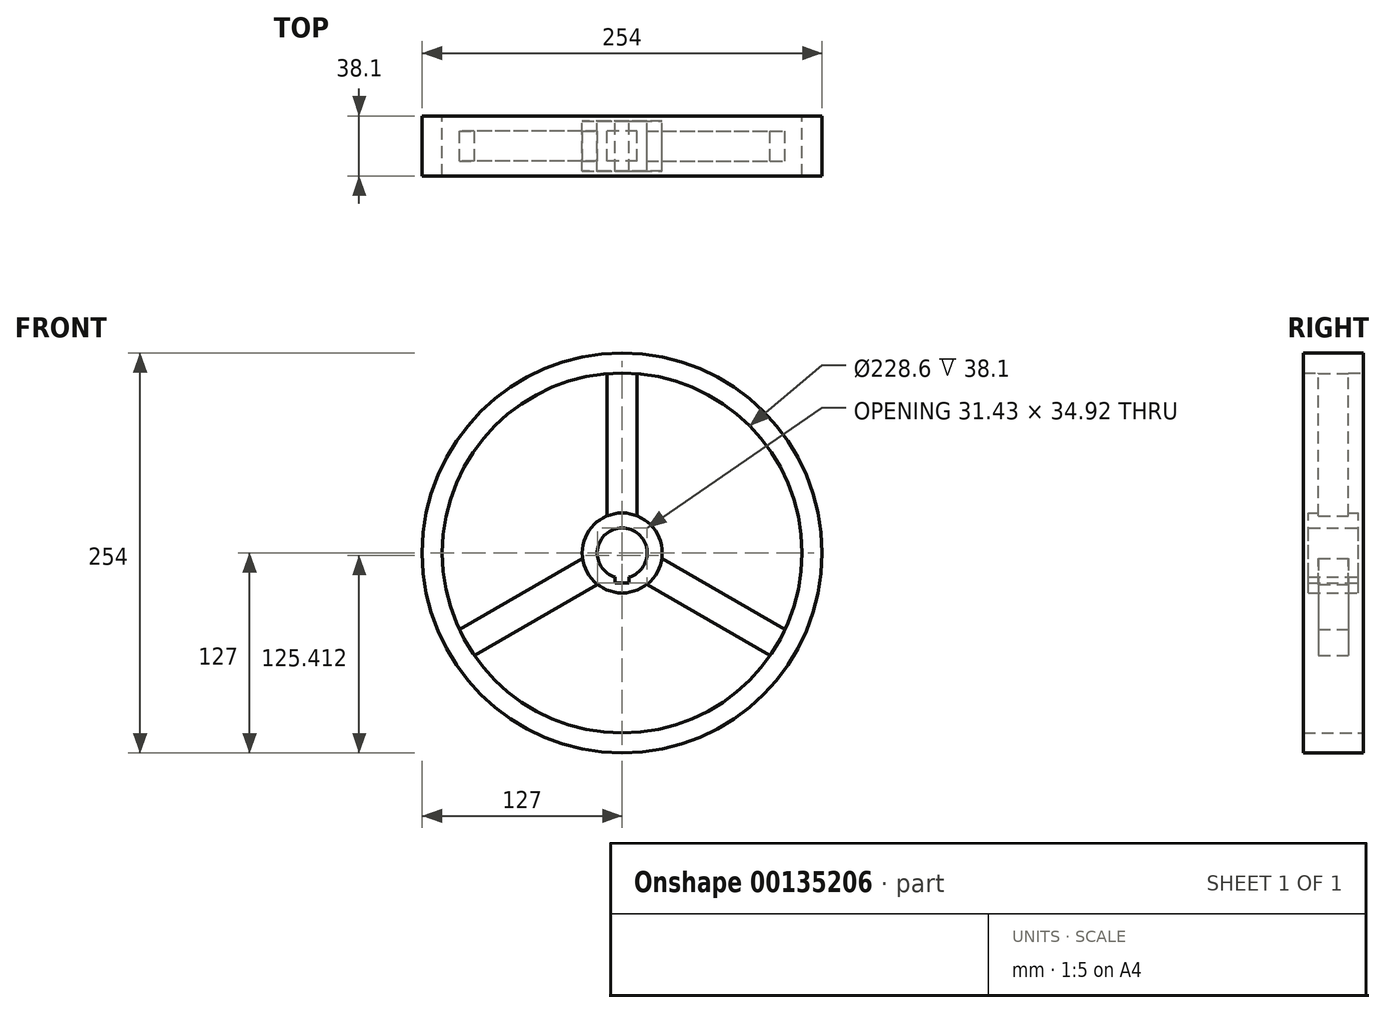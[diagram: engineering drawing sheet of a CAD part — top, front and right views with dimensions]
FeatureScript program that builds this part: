
annotation { "Feature Type Name" : "Feature", "Feature Type Description" : "" }
export const myFeature = defineFeature(function(context is Context, id is Id, definition is map)
    precondition{}
    {
        {
            var Q0;
            Q0=qCreatedBy(makeId("Front.planeOp"),FACE);
            var sketch = newSketch(context, id + "F0", { "sketchPlane" : qUnion([Q0])});
            skCircle(sketch, "E0", {"center": v(0, 0) * mm, "radius": 127 * mm});
            skCircle(sketch, "E1", {"center": v(0, 0) * mm, "radius": 114.3 * mm});
            skCircle(sketch, "E2", {"center": v(0, 0) * mm, "radius": 25.4 * mm});
            skArc(sketch, "E3", {"start": v(4.45, -15.24) * mm, "mid": v(0, 15.88) * mm, "end": v(-4.45, -15.24) * mm});
            skLineSegment(sketch, "E4", {"start": v(-9.53, 23.55) * mm, "end": v(-9.53, 113.9) * mm});
            skLineSegment(sketch, "E5", {"start": v(9.52, 23.55) * mm, "end": v(9.52, 113.9) * mm});
            skLineSegment(sketch, "E6", {"start": v(-25.15, -3.52) * mm, "end": v(-103.4, -48.7) * mm});
            skLineSegment(sketch, "E7", {"start": v(-15.63, -20.02) * mm, "end": v(-93.88, -65.2) * mm});
            skLineSegment(sketch, "E8", {"start": v(25.15, -3.52) * mm, "end": v(103.4, -48.7) * mm});
            skLineSegment(sketch, "E9", {"start": v(15.63, -20.02) * mm, "end": v(93.88, -65.2) * mm});
            skLineSegment(sketch, "E10", {"start": v(-4.45, -15.24) * mm, "end": v(-4.45, -19.05) * mm});
            skLineSegment(sketch, "E11", {"start": v(-4.44, -19.05) * mm, "end": v(4.45, -19.05) * mm});
            skLineSegment(sketch, "E12", {"start": v(4.45, -19.05) * mm, "end": v(4.45, -15.24) * mm});
            skSolve(sketch);
        }
        {
            var Q0;
            Q0 = qSketchRegion(id + "F0", true);
            extrude(context, id + "F1", {"entities" : qUnion([Q0]), "endBound" : BoundingType.SYMMETRIC, "depth" : 38.1 * mm});
        }
        {
            var Q0;
            {var subQ0=sQuery(id+"F0.wireOp",EDGE,"E4");Q0=makeQuery(id+"F0.imprint","IMPRINT",FACE,{"disambiguationData":[TD([[makeQuery(id+"F0.imprint","IMPRINT",EDGE,{"derivedFrom":subQ0}),-1.0]])]});}
            var Q1;
            {var subQ0=sQuery(id+"F0.wireOp",EDGE,"E6");Q1=makeQuery(id+"F0.imprint","IMPRINT",FACE,{"disambiguationData":[TD([[makeQuery(id+"F0.imprint","IMPRINT",EDGE,{"derivedFrom":subQ0}),1.0]])]});}
            var Q2;
            {var subQ0=sQuery(id+"F0.wireOp",EDGE,"E8");Q2=makeQuery(id+"F0.imprint","IMPRINT",FACE,{"disambiguationData":[TD([[makeQuery(id+"F0.imprint","IMPRINT",EDGE,{"derivedFrom":subQ0}),-1.0]])]});}
            extrude(context, id + "F2", {"entities" : qUnion([Q0, Q1, Q2]), "operationType" : NewBodyOperationType.ADD, "endBound" : BoundingType.SYMMETRIC, "depth" : 19.05 * mm});
        }
        {
            var Q0;
            Q0=makeQuery(id+"F0.imprint","IMPRINT",FACE,{"disambiguationData":[TD([[makeQuery(id+"F0.imprint","IMPRINT",EDGE,{"derivedFrom":sQuery(id+"F0.wireOp",EDGE,"E3")}),-1.0]])]});
            extrude(context, id + "F3", {"entities" : qUnion([Q0]), "operationType" : NewBodyOperationType.ADD, "endBound" : BoundingType.SYMMETRIC, "depth" : 31.75 * mm});
        }
    });
